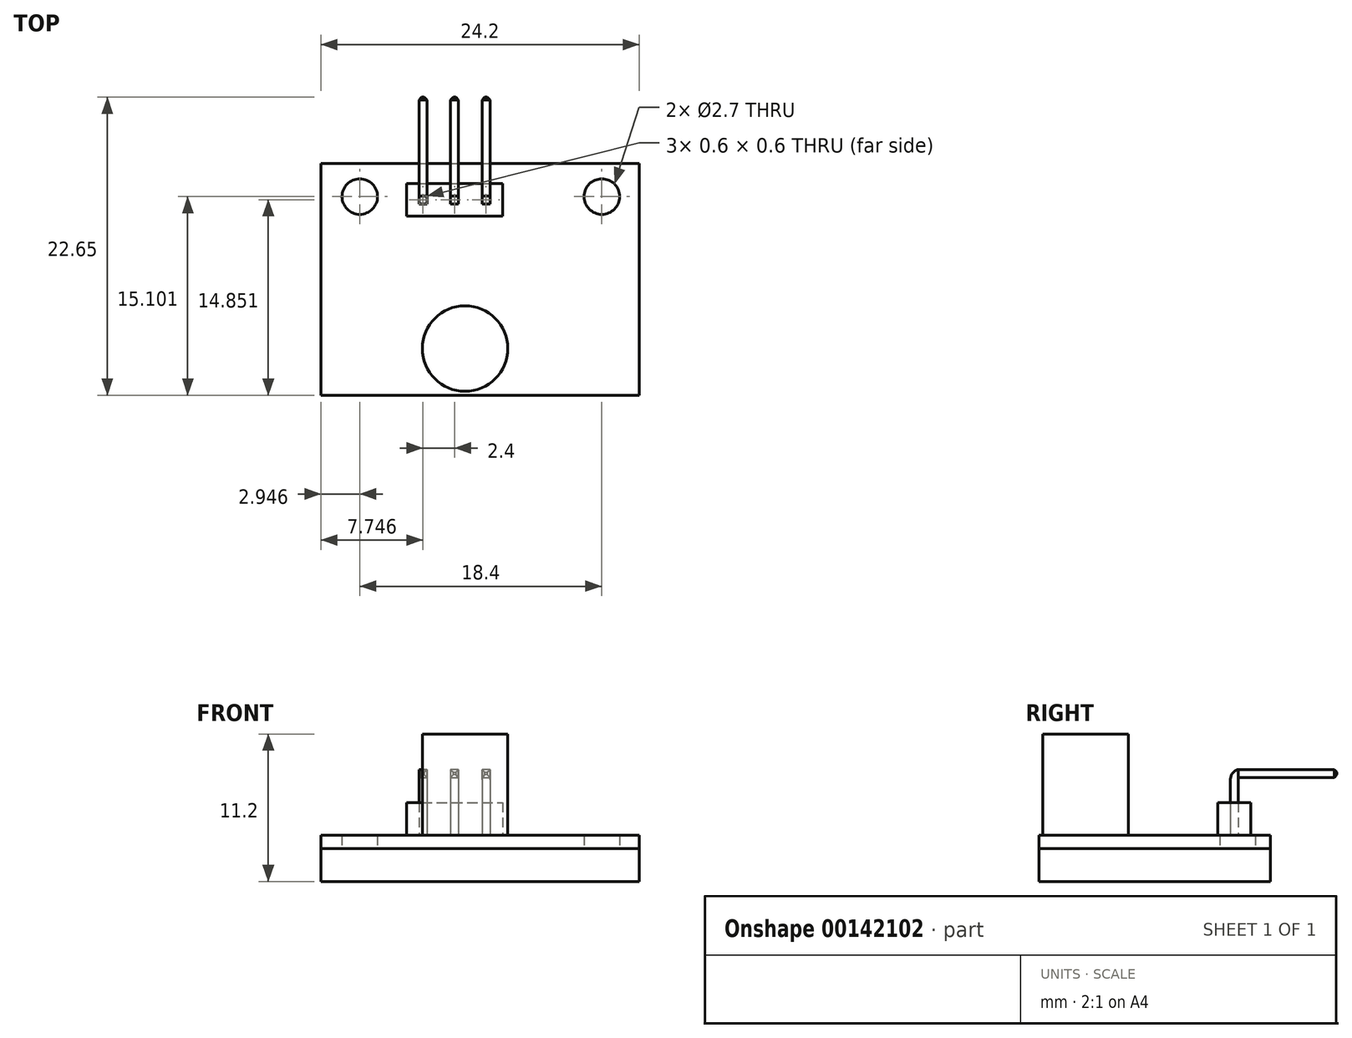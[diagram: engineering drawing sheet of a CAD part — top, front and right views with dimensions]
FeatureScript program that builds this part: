
annotation { "Feature Type Name" : "Feature", "Feature Type Description" : "" }
export const myFeature = defineFeature(function(context is Context, id is Id, definition is map)
    precondition{}
    {
        {
            var Q0;
            Q0=qCreatedBy(makeId("Top.planeOp"),FACE);
            var sketch = newSketch(context, id + "F0", { "sketchPlane" : qUnion([Q0])});
            skLineSegment(sketch, "E0.bottom", {"start": v(-12.56, 8.31) * mm, "end": v(11.64, 8.31) * mm});
            skLineSegment(sketch, "E0.top", {"start": v(-12.56, -9.29) * mm, "end": v(11.64, -9.29) * mm});
            skLineSegment(sketch, "E0.left", {"start": v(-12.56, 8.31) * mm, "end": v(-12.56, -9.29) * mm});
            skLineSegment(sketch, "E0.right", {"start": v(11.64, 8.31) * mm, "end": v(11.64, -9.29) * mm});
            skCircle(sketch, "E1", {"center": v(8.79, 5.81) * mm, "radius": 1.35 * mm});
            skCircle(sketch, "E2", {"center": v(-9.61, 5.81) * mm, "radius": 1.35 * mm});
            skSolve(sketch);
        }
        {
            var Q0;
            Q0=makeQuery(id+"F0.imprint","IMPRINT",FACE,{"disambiguationData":[TD([[makeQuery(id+"F0.imprint","IMPRINT",EDGE,{"derivedFrom":sQuery(id+"F0.wireOp",EDGE,"E0.bottom")}),-1.0]])]});
            extrude(context, id + "F1", {"entities" : qUnion([Q0]), "depth" : 1 * mm});
        }
        {
            var Q0;
            Q0=makeQuery(id+"F1.opExtrude","CAP_FACE",FACE,{"disambiguationData":[OSD([sQuery(id+"F0.wireOp",EDGE,"E0.bottom"),sQuery(id+"F0.wireOp",EDGE,"E0.top"),sQuery(id+"F0.wireOp",EDGE,"E0.left"),sQuery(id+"F0.wireOp",EDGE,"E0.right"),sQuery(id+"F0.wireOp",EDGE,"E1"),sQuery(id+"F0.wireOp",EDGE,"E2")])],"isStart":false});
            var sketch = newSketch(context, id + "F2", { "sketchPlane" : qUnion([Q0])});
            skLineSegment(sketch, "E3.bottom", {"start": v(-6.06, 6.81) * mm, "end": v(1.24, 6.81) * mm});
            skLineSegment(sketch, "E3.top", {"start": v(-6.06, 4.31) * mm, "end": v(1.24, 4.31) * mm});
            skLineSegment(sketch, "E3.left", {"start": v(-6.06, 6.81) * mm, "end": v(-6.06, 4.31) * mm});
            skLineSegment(sketch, "E3.right", {"start": v(1.24, 6.81) * mm, "end": v(1.24, 4.31) * mm});
            skLineSegment(sketch, "E4.bottom", {"start": v(-5.11, 5.86) * mm, "end": v(-4.51, 5.86) * mm});
            skLineSegment(sketch, "E4.top", {"start": v(-5.11, 5.26) * mm, "end": v(-4.51, 5.26) * mm});
            skLineSegment(sketch, "E4.left", {"start": v(-5.11, 5.86) * mm, "end": v(-5.11, 5.26) * mm});
            skLineSegment(sketch, "E4.right", {"start": v(-4.51, 5.86) * mm, "end": v(-4.51, 5.26) * mm});
            skLineSegment(sketch, "E5.bottom", {"start": v(-2.71, 5.86) * mm, "end": v(-2.11, 5.86) * mm});
            skLineSegment(sketch, "E5.top", {"start": v(-2.71, 5.26) * mm, "end": v(-2.11, 5.26) * mm});
            skLineSegment(sketch, "E5.left", {"start": v(-2.71, 5.86) * mm, "end": v(-2.71, 5.26) * mm});
            skLineSegment(sketch, "E5.right", {"start": v(-2.11, 5.86) * mm, "end": v(-2.11, 5.26) * mm});
            skLineSegment(sketch, "E6.bottom", {"start": v(-0.31, 5.86) * mm, "end": v(0.29, 5.86) * mm});
            skLineSegment(sketch, "E6.top", {"start": v(-0.31, 5.26) * mm, "end": v(0.29, 5.26) * mm});
            skLineSegment(sketch, "E6.left", {"start": v(-0.31, 5.86) * mm, "end": v(-0.31, 5.26) * mm});
            skLineSegment(sketch, "E6.right", {"start": v(0.29, 5.86) * mm, "end": v(0.29, 5.26) * mm});
            skSolve(sketch);
        }
        {
            var Q0;
            Q0=makeQuery(id+"F2.imprint","IMPRINT",FACE,{"disambiguationData":[TD([[makeQuery(id+"F2.imprint","IMPRINT",EDGE,{"derivedFrom":sQuery(id+"F2.wireOp",EDGE,"E3.bottom")}),-1.0]])]});
            extrude(context, id + "F3", {"entities" : qUnion([Q0]), "depth" : 2.5 * mm});
        }
        {
            var Q0;
            Q0=makeQuery(id+"F1.opExtrude","CAP_FACE",FACE,{"disambiguationData":[OSD([sQuery(id+"F0.wireOp",EDGE,"E0.bottom"),sQuery(id+"F0.wireOp",EDGE,"E0.top"),sQuery(id+"F0.wireOp",EDGE,"E0.left"),sQuery(id+"F0.wireOp",EDGE,"E0.right"),sQuery(id+"F0.wireOp",EDGE,"E1"),sQuery(id+"F0.wireOp",EDGE,"E2")])],"isStart":false});
            var sketch = newSketch(context, id + "F4", { "sketchPlane" : qUnion([Q0])});
            skLineSegment(sketch, "E7.bottom", {"start": v(-5.11, 5.86) * mm, "end": v(-4.51, 5.86) * mm});
            skLineSegment(sketch, "E7.top", {"start": v(-5.11, 5.26) * mm, "end": v(-4.51, 5.26) * mm});
            skLineSegment(sketch, "E7.left", {"start": v(-5.11, 5.86) * mm, "end": v(-5.11, 5.26) * mm});
            skLineSegment(sketch, "E7.right", {"start": v(-4.51, 5.86) * mm, "end": v(-4.51, 5.26) * mm});
            skLineSegment(sketch, "E8.bottom", {"start": v(-2.71, 5.86) * mm, "end": v(-2.11, 5.86) * mm});
            skLineSegment(sketch, "E8.top", {"start": v(-2.71, 5.26) * mm, "end": v(-2.11, 5.26) * mm});
            skLineSegment(sketch, "E8.left", {"start": v(-2.71, 5.86) * mm, "end": v(-2.71, 5.26) * mm});
            skLineSegment(sketch, "E8.right", {"start": v(-2.11, 5.86) * mm, "end": v(-2.11, 5.26) * mm});
            skLineSegment(sketch, "E9.bottom", {"start": v(0.29, 5.26) * mm, "end": v(-0.31, 5.26) * mm});
            skLineSegment(sketch, "E9.top", {"start": v(0.29, 5.86) * mm, "end": v(-0.31, 5.86) * mm});
            skLineSegment(sketch, "E9.left", {"start": v(0.29, 5.26) * mm, "end": v(0.29, 5.86) * mm});
            skLineSegment(sketch, "E9.right", {"start": v(-0.31, 5.26) * mm, "end": v(-0.31, 5.86) * mm});
            skSolve(sketch);
        }
        {
            var Q0;
            Q0=makeQuery(id+"F4.imprint","IMPRINT",FACE,{"disambiguationData":[TD([[makeQuery(id+"F4.imprint","IMPRINT",EDGE,{"derivedFrom":sQuery(id+"F4.wireOp",EDGE,"E7.bottom")}),-1.0]])]});
            var Q1;
            Q1=makeQuery(id+"F4.imprint","IMPRINT",FACE,{"disambiguationData":[TD([[makeQuery(id+"F4.imprint","IMPRINT",EDGE,{"derivedFrom":sQuery(id+"F4.wireOp",EDGE,"E8.bottom")}),-1.0]])]});
            var Q2;
            Q2=makeQuery(id+"F4.imprint","IMPRINT",FACE,{"disambiguationData":[TD([[makeQuery(id+"F4.imprint","IMPRINT",EDGE,{"derivedFrom":sQuery(id+"F4.wireOp",EDGE,"E9.bottom")}),-1.0]])]});
            extrude(context, id + "F5", {"entities" : qUnion([Q0, Q1, Q2]), "depth" : 5 * mm});
        }
        {
            var Q0;
            Q0=makeQuery(id+"F5.opExtrude","SWEPT_FACE",FACE,{"disambiguationData":[OSD([sQuery(id+"F4.wireOp",EDGE,"E9.top")])]});
            var sketch = newSketch(context, id + "F6", { "sketchPlane" : qUnion([Q0])});
            skLineSegment(sketch, "E10.bottom", {"start": v(-0.29, 6) * mm, "end": v(0.31, 6) * mm});
            skLineSegment(sketch, "E10.top", {"start": v(-0.29, 5.4) * mm, "end": v(0.31, 5.4) * mm});
            skLineSegment(sketch, "E10.left", {"start": v(-0.29, 6) * mm, "end": v(-0.29, 5.4) * mm});
            skLineSegment(sketch, "E10.right", {"start": v(0.31, 6) * mm, "end": v(0.31, 5.4) * mm});
            skLineSegment(sketch, "E11.bottom", {"start": v(2.11, 6) * mm, "end": v(2.71, 6) * mm});
            skLineSegment(sketch, "E11.top", {"start": v(2.11, 5.4) * mm, "end": v(2.71, 5.4) * mm});
            skLineSegment(sketch, "E11.left", {"start": v(2.11, 6) * mm, "end": v(2.11, 5.4) * mm});
            skLineSegment(sketch, "E11.right", {"start": v(2.71, 6) * mm, "end": v(2.71, 5.4) * mm});
            skLineSegment(sketch, "E12.bottom", {"start": v(4.51, 6) * mm, "end": v(5.11, 6) * mm});
            skLineSegment(sketch, "E12.top", {"start": v(4.51, 5.4) * mm, "end": v(5.11, 5.4) * mm});
            skLineSegment(sketch, "E12.left", {"start": v(4.51, 6) * mm, "end": v(4.51, 5.4) * mm});
            skLineSegment(sketch, "E12.right", {"start": v(5.11, 6) * mm, "end": v(5.11, 5.4) * mm});
            skSolve(sketch);
        }
        {
            var Q0;
            Q0=makeQuery(id+"F6.imprint","IMPRINT",FACE,{"disambiguationData":[TD([[makeQuery(id+"F6.imprint","IMPRINT",EDGE,{"derivedFrom":sQuery(id+"F6.wireOp",EDGE,"E10.bottom")}),-1.0]])]});
            var Q1;
            Q1=makeQuery(id+"F6.imprint","IMPRINT",FACE,{"disambiguationData":[TD([[makeQuery(id+"F6.imprint","IMPRINT",EDGE,{"derivedFrom":sQuery(id+"F6.wireOp",EDGE,"E11.bottom")}),-1.0]])]});
            var Q2;
            Q2=makeQuery(id+"F6.imprint","IMPRINT",FACE,{"disambiguationData":[TD([[makeQuery(id+"F6.imprint","IMPRINT",EDGE,{"derivedFrom":sQuery(id+"F6.wireOp",EDGE,"E12.bottom")}),-1.0]])]});
            extrude(context, id + "F7", {"entities" : qUnion([Q0, Q1, Q2]), "depth" : 7.5 * mm});
        }
        {
            var Q0;
            Q0=makeQuery(id+"F5.opExtrude","CAP_EDGE",EDGE,{"disambiguationData":[OSD([sQuery(id+"F4.wireOp",EDGE,"E9.bottom")])],"isStart":false});
            var Q1;
            Q1=makeQuery(id+"F5.opExtrude","CAP_EDGE",EDGE,{"disambiguationData":[OSD([sQuery(id+"F4.wireOp",EDGE,"E8.top")])],"isStart":false});
            var Q2;
            Q2=makeQuery(id+"F5.opExtrude","CAP_EDGE",EDGE,{"disambiguationData":[OSD([sQuery(id+"F4.wireOp",EDGE,"E7.top")])],"isStart":false});
            fillet(context, id + "F8", {"entities" : qUnion([Q0, Q1, Q2]), "radius" : 0.78 * mm, "tangentPropagation" : true, "allowEdgeOverflow" : false});
        }
        {
            var Q0;
            Q0=makeQuery(id+"F7.opExtrude","CAP_EDGE",EDGE,{"disambiguationData":[OSD([sQuery(id+"F6.wireOp",EDGE,"E10.bottom")])],"isStart":false});
            var Q1;
            Q1=makeQuery(id+"F7.opExtrude","CAP_EDGE",EDGE,{"disambiguationData":[OSD([sQuery(id+"F6.wireOp",EDGE,"E10.top")])],"isStart":false});
            var Q2;
            Q2=makeQuery(id+"F7.opExtrude","CAP_EDGE",EDGE,{"disambiguationData":[OSD([sQuery(id+"F6.wireOp",EDGE,"E10.left")])],"isStart":false});
            var Q3;
            Q3=makeQuery(id+"F7.opExtrude","CAP_EDGE",EDGE,{"disambiguationData":[OSD([sQuery(id+"F6.wireOp",EDGE,"E10.right")])],"isStart":false});
            var Q4;
            Q4=makeQuery(id+"F7.opExtrude","CAP_EDGE",EDGE,{"disambiguationData":[OSD([sQuery(id+"F6.wireOp",EDGE,"E11.left")])],"isStart":false});
            var Q5;
            Q5=makeQuery(id+"F7.opExtrude","CAP_EDGE",EDGE,{"disambiguationData":[OSD([sQuery(id+"F6.wireOp",EDGE,"E11.bottom")])],"isStart":false});
            var Q6;
            Q6=makeQuery(id+"F7.opExtrude","CAP_EDGE",EDGE,{"disambiguationData":[OSD([sQuery(id+"F6.wireOp",EDGE,"E11.top")])],"isStart":false});
            var Q7;
            Q7=makeQuery(id+"F7.opExtrude","CAP_EDGE",EDGE,{"disambiguationData":[OSD([sQuery(id+"F6.wireOp",EDGE,"E11.right")])],"isStart":false});
            var Q8;
            Q8=makeQuery(id+"F7.opExtrude","CAP_EDGE",EDGE,{"disambiguationData":[OSD([sQuery(id+"F6.wireOp",EDGE,"E12.bottom")])],"isStart":false});
            var Q9;
            Q9=makeQuery(id+"F7.opExtrude","CAP_EDGE",EDGE,{"disambiguationData":[OSD([sQuery(id+"F6.wireOp",EDGE,"E12.left")])],"isStart":false});
            var Q10;
            Q10=makeQuery(id+"F7.opExtrude","CAP_EDGE",EDGE,{"disambiguationData":[OSD([sQuery(id+"F6.wireOp",EDGE,"E12.top")])],"isStart":false});
            var Q11;
            Q11=makeQuery(id+"F7.opExtrude","CAP_EDGE",EDGE,{"disambiguationData":[OSD([sQuery(id+"F6.wireOp",EDGE,"E12.right")])],"isStart":false});
            chamfer(context, id + "F9", {"entities" : qUnion([Q0, Q1, Q2, Q3, Q4, Q5, Q6, Q7, Q8, Q9, Q10, Q11]), "width" : 0.2 * mm, "tangentPropagation" : true});
        }
        {
            var Q0;
            Q0=makeQuery(id+"F1.opExtrude","CAP_FACE",FACE,{"disambiguationData":[OSD([sQuery(id+"F0.wireOp",EDGE,"E0.bottom"),sQuery(id+"F0.wireOp",EDGE,"E0.top"),sQuery(id+"F0.wireOp",EDGE,"E0.left"),sQuery(id+"F0.wireOp",EDGE,"E0.right"),sQuery(id+"F0.wireOp",EDGE,"E1"),sQuery(id+"F0.wireOp",EDGE,"E2")])],"isStart":false});
            var sketch = newSketch(context, id + "F10", { "sketchPlane" : qUnion([Q0])});
            skCircle(sketch, "E13", {"center": v(-1.61, -5.74) * mm, "radius": 3.25 * mm});
            skSolve(sketch);
        }
        {
            var Q0;
            Q0=makeQuery(id+"F10.imprint","IMPRINT",FACE,{"disambiguationData":[TD([[makeQuery(id+"F10.imprint","IMPRINT",EDGE,{"derivedFrom":sQuery(id+"F10.wireOp",EDGE,"E13")}),1.0]])]});
            extrude(context, id + "F11", {"entities" : qUnion([Q0]), "depth" : 7.7 * mm});
        }
        {
            var Q0;
            Q0=makeQuery(id+"F1.opExtrude","CAP_FACE",FACE,{"disambiguationData":[OSD([sQuery(id+"F0.wireOp",EDGE,"E0.bottom"),sQuery(id+"F0.wireOp",EDGE,"E0.top"),sQuery(id+"F0.wireOp",EDGE,"E0.left"),sQuery(id+"F0.wireOp",EDGE,"E0.right"),sQuery(id+"F0.wireOp",EDGE,"E1"),sQuery(id+"F0.wireOp",EDGE,"E2")])],"isStart":true});
            var sketch = newSketch(context, id + "F12", { "sketchPlane" : qUnion([Q0])});
            skLineSegment(sketch, "E14.bottom", {"start": v(-12.56, 9.29) * mm, "end": v(11.64, 9.29) * mm});
            skLineSegment(sketch, "E14.top", {"start": v(-12.56, -8.31) * mm, "end": v(11.64, -8.31) * mm});
            skLineSegment(sketch, "E14.left", {"start": v(-12.56, 9.29) * mm, "end": v(-12.56, -8.31) * mm});
            skLineSegment(sketch, "E14.right", {"start": v(11.64, 9.29) * mm, "end": v(11.64, -8.31) * mm});
            skSolve(sketch);
        }
        {
            var Q0;
            Q0=makeQuery(id+"F12.imprint","IMPRINT",FACE,{"disambiguationData":[TD([[makeQuery(id+"F12.imprint","IMPRINT",EDGE,{"derivedFrom":sQuery(id+"F12.wireOp",EDGE,"E14.bottom")}),-1.0]])]});
            var Q1;
            Q1=makeQuery(id+"F12.imprint","IMPRINT",FACE,{"disambiguationData":[TD([[makeQuery(id+"F12.imprint","IMPRINT",EDGE,{"derivedFrom":makeQuery(id+"F1.opExtrude","CAP_EDGE",EDGE,{"disambiguationData":[OSD([sQuery(id+"F0.wireOp",EDGE,"E1")])],"isStart":true})}),-1.0]])]});
            var Q2;
            Q2=makeQuery(id+"F12.imprint","IMPRINT",FACE,{"disambiguationData":[TD([[makeQuery(id+"F12.imprint","IMPRINT",EDGE,{"derivedFrom":makeQuery(id+"F1.opExtrude","CAP_EDGE",EDGE,{"disambiguationData":[OSD([sQuery(id+"F0.wireOp",EDGE,"E2")])],"isStart":true})}),-1.0]])]});
            extrude(context, id + "F13", {"entities" : qUnion([Q0, Q1, Q2]), "depth" : 2.5 * mm});
        }
    });
